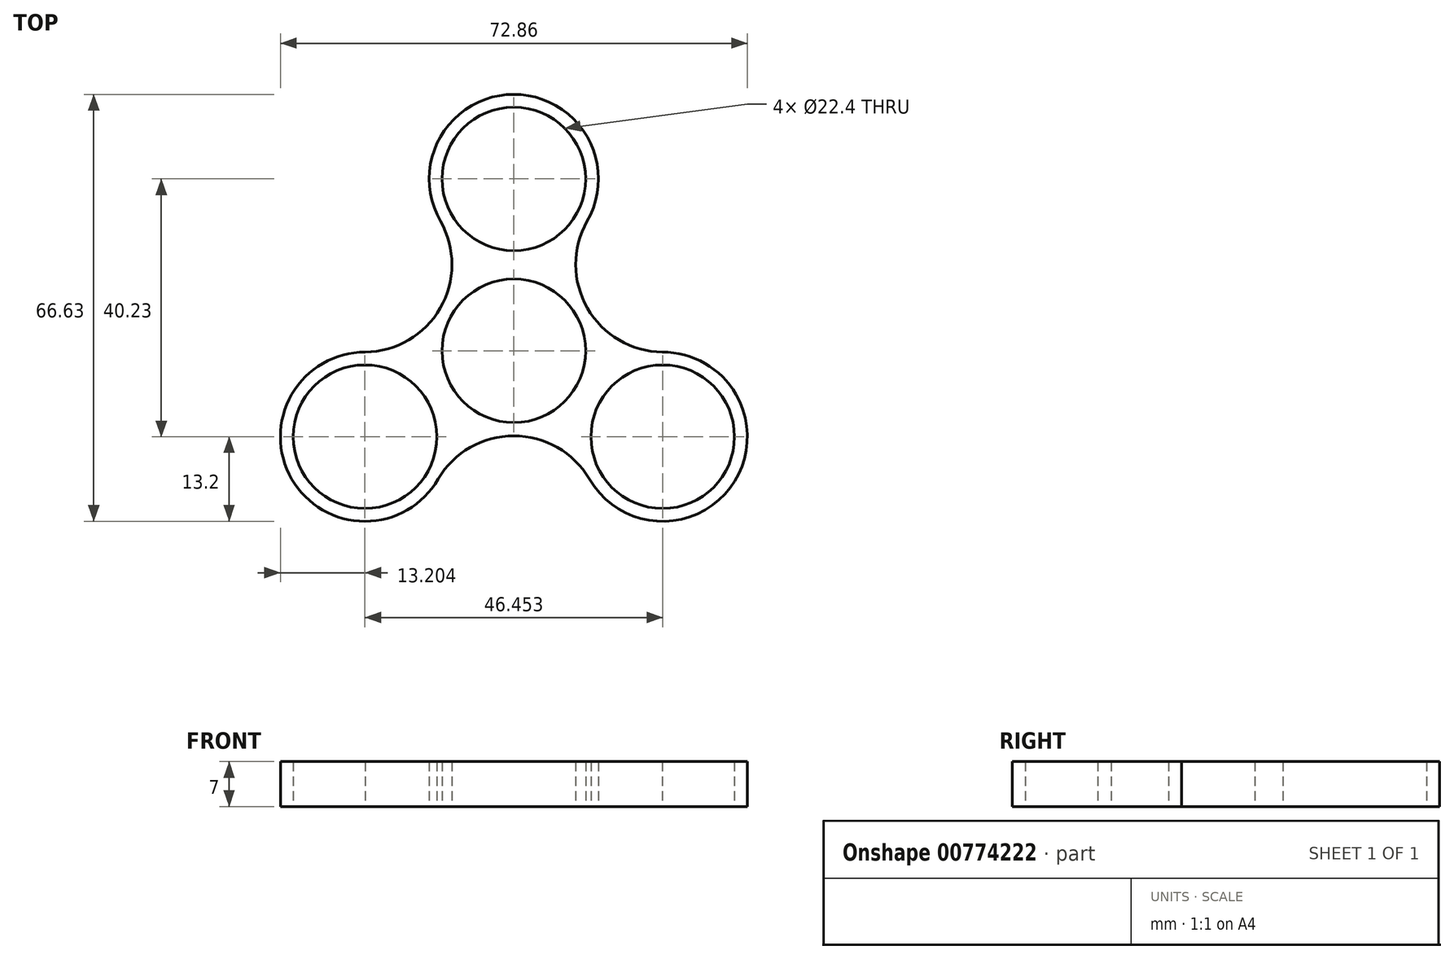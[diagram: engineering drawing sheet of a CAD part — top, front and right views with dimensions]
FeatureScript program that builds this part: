
annotation { "Feature Type Name" : "Feature", "Feature Type Description" : "" }
export const myFeature = defineFeature(function(context is Context, id is Id, definition is map)
    precondition{}
    {
        {
            var Q0;
            Q0=qCreatedBy(makeId("Top.planeOp"),FACE);
            var sketch = newSketch(context, id + "F0", { "sketchPlane" : qUnion([Q0])});
            skCircle(sketch, "E0", {"center": v(0, 0) * mm, "radius": 11.2 * mm});
            skCircle(sketch, "E1", {"center": v(0, 26.82) * mm, "radius": 11.2 * mm});
            skArc(sketch, "E2", {"start": v(11.43, 20.22) * mm, "mid": v(0, 40.02) * mm, "end": v(-11.43, 20.22) * mm});
            skCircle(sketch, "E3.1.0", {"center": v(-23.23, -13.41) * mm, "radius": 11.2 * mm});
            skArc(sketch, "E3.1.1", {"start": v(-23.18, -0.21) * mm, "mid": v(-34.67, -20) * mm, "end": v(-11.8, -20.01) * mm});
            skCircle(sketch, "E3.2.0", {"center": v(23.23, -13.4) * mm, "radius": 11.2 * mm});
            skArc(sketch, "E3.2.1", {"start": v(11.8, -20.01) * mm, "mid": v(34.67, -20) * mm, "end": v(23.19, -0.2) * mm});
            skArc(sketch, "E4.2.0", {"start": v(-23.23, -0.21) * mm, "mid": v(-34.66, -20.01) * mm, "end": v(-11.8, -20.01) * mm});
            skArc(sketch, "E4.4.0", {"start": v(11.8, -20.01) * mm, "mid": v(34.66, -20.01) * mm, "end": v(23.23, -0.21) * mm});
            skArc(sketch, "E5", {"start": v(11.43, 20.22) * mm, "mid": v(11.5, 6.63) * mm, "end": v(23.23, -0.21) * mm});
            skArc(sketch, "E6.1.0", {"start": v(-23.18, -0.21) * mm, "mid": v(-11.48, 6.65) * mm, "end": v(-11.43, 20.22) * mm});
            skArc(sketch, "E6.2.0", {"start": v(11.8, -20.01) * mm, "mid": v(0, -13.27) * mm, "end": v(-11.8, -20.01) * mm});
            skSolve(sketch);
        }
        {
            var Q0;
            Q0=qSketchRegion(id+"F0",true);
            extrude(context, id + "F1", {"entities" : qUnion([Q0]), "depth" : 7 * mm, "offsetDistance" : 25 * mm});
        }
    });
